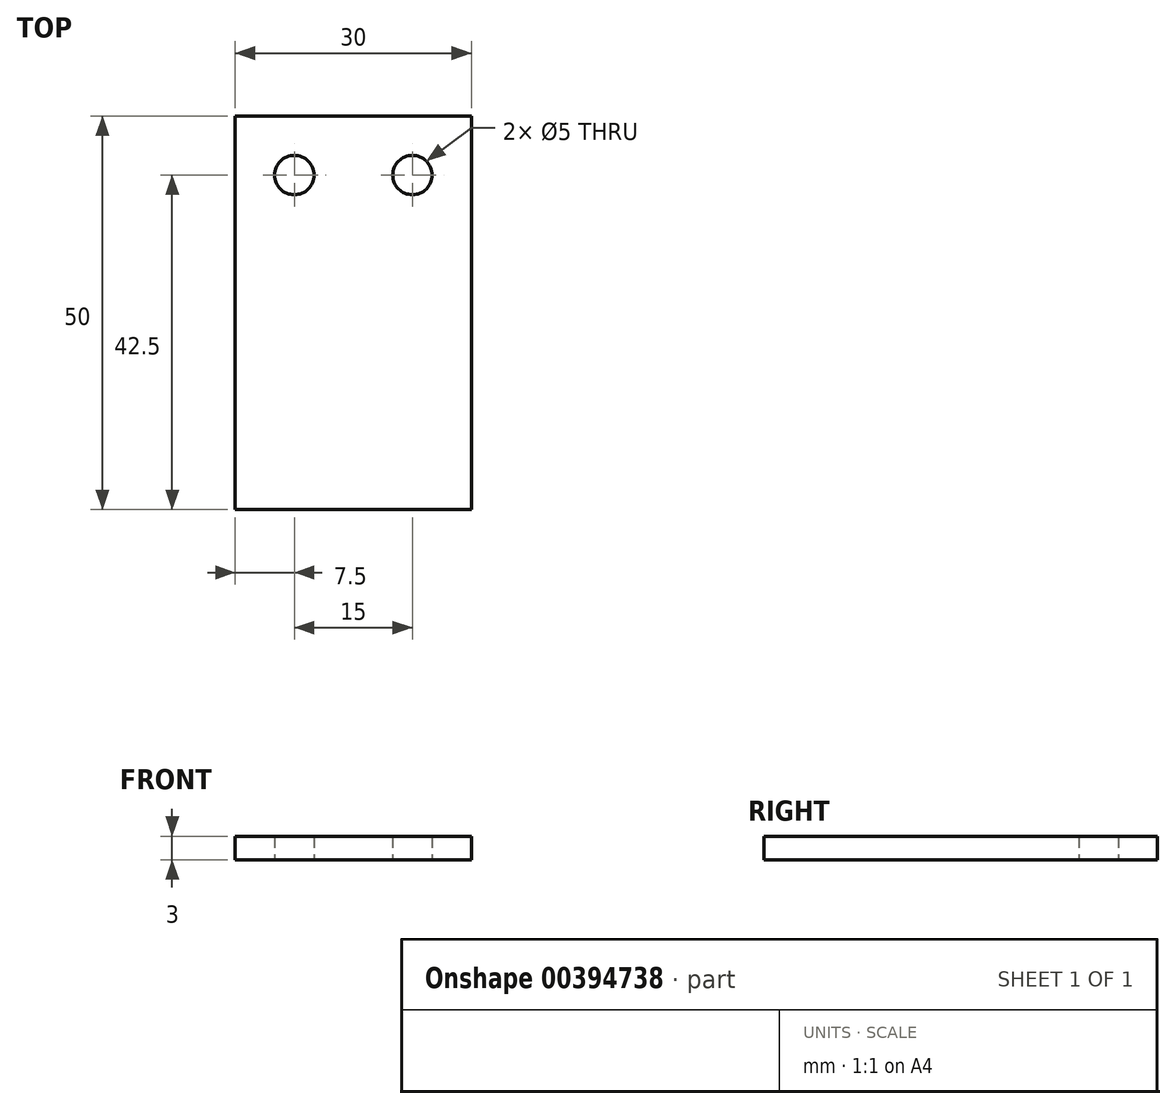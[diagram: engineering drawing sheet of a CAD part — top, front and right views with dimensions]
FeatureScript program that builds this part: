
annotation { "Feature Type Name" : "Feature", "Feature Type Description" : "" }
export const myFeature = defineFeature(function(context is Context, id is Id, definition is map)
    precondition{}
    {
        {
            var Q0;
            Q0=qCreatedBy(makeId("Top.planeOp"),FACE);
            var sketch = newSketch(context, id + "F0", { "sketchPlane" : qUnion([Q0])});
            skLineSegment(sketch, "E0.bottom", {"start": v(15, 25) * mm, "end": v(-15, 25) * mm});
            skLineSegment(sketch, "E0.top", {"start": v(15, -25) * mm, "end": v(-15, -25) * mm});
            skLineSegment(sketch, "E0.left", {"start": v(15, 25) * mm, "end": v(15, -25) * mm});
            skLineSegment(sketch, "E0.right", {"start": v(-15, 25) * mm, "end": v(-15, -25) * mm});
            skPoint(sketch, "E0.middle", {"position": v(0, 0) * mm});
            skCircle(sketch, "E1", {"center": v(-7.5, 17.5) * mm, "radius": 2.5 * mm});
            skCircle(sketch, "E2", {"center": v(7.5, 17.5) * mm, "radius": 2.5 * mm});
            skLineSegment(sketch, "E3", {"start": v(-7.5, 17.5) * mm, "end": v(7.5, 17.5) * mm, "construction": true});
            skLineSegment(sketch, "E4", {"start": v(7.5, 20) * mm, "end": v(7.5, 25) * mm, "construction": true});
            skLineSegment(sketch, "E5", {"start": v(10, 17.5) * mm, "end": v(15, 17.5) * mm, "construction": true});
            skLineSegment(sketch, "E6", {"start": v(-10, 17.5) * mm, "end": v(-15, 17.5) * mm, "construction": true});
            skSolve(sketch);
        }
        {
            var Q0;
            Q0=makeQuery(id+"F0.imprint","IMPRINT",FACE,{"disambiguationData":[TD([[makeQuery(id+"F0.imprint","IMPRINT",EDGE,{"derivedFrom":sQuery(id+"F0.wireOp",EDGE,"E0.bottom")}),1.0]])]});
            extrude(context, id + "F1", {"entities" : qUnion([Q0]), "depth" : 3 * mm});
        }
    });
